# Revit family: EVE-Series
name_source: partatom
category: Lighting Fixtures
revit_build: Autodesk Revit MEP 2012 (Build: 20110309_2315(x64)
units: mm (PartAtom-declared; Revit-internal decimal feet)

## types (4) — shared parameters
Default Elevation = 48.000"
Description = The EVE Series is a compact architectural LED exit sign designed for fast installation and reliable service
Glass = Hubbell - light Glass
Lamp = Long-Life LEDs
Load Classification = Lighting
Manufacturer = Dual Lighting
Manufacturer Fax = (866)-898-0131
Model = EVE Series
Product Documentation Link = http://cdn.dual-lite.com
Product Page URL = http://www.dual-lite.com
URL = http://www.dual-lite.com
Voltage = 120 V
Wattage Comments = 6 or 12 Watts

## per-type parameters (varying)
| type | Apparent Load | Finish | Lens |
| EVE -  White with Red Exit | 1 VA | Hubbell - Paint - White | Hubbell - Red Glass |
| EVE - Black with Green Exit | 0 VA | Hubbell - Paint - Black | Hubbell - Green Glass |
| EVE - Black with Red Exit | 0 VA | Hubbell - Paint - Black | Hubbell - Red Glass |
| EVE -  White with Green Exit | 1 VA | Hubbell - Paint - White | Hubbell - Green Glass |

## geometry (parser evidence)
native form markers: Sweep x5
no freeform markers — native parametric forms only
